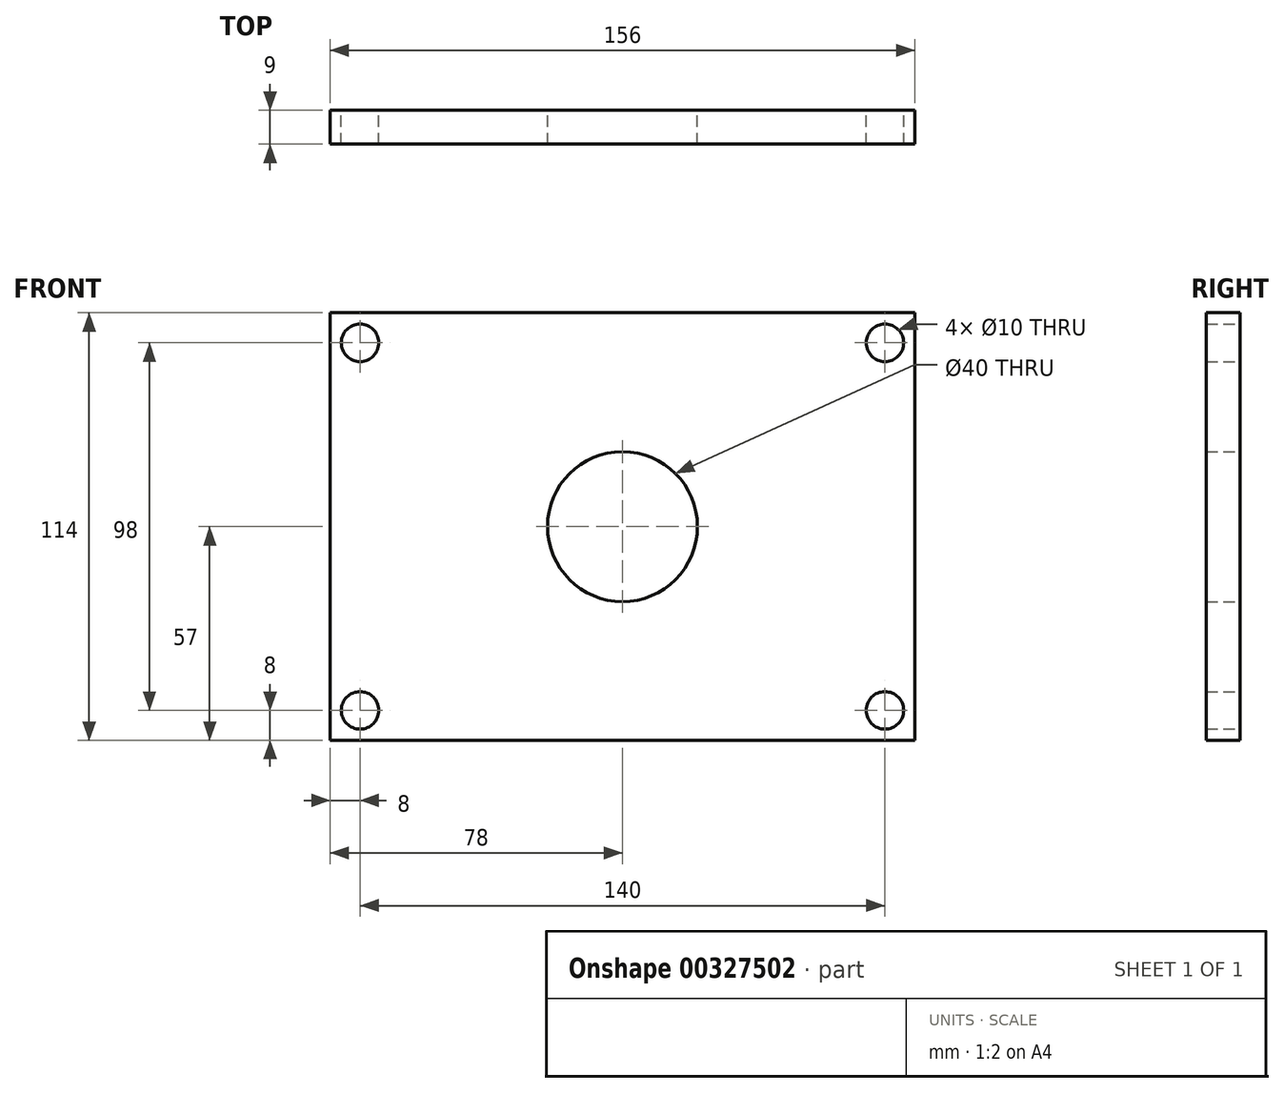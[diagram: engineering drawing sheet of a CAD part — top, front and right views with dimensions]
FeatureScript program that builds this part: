
annotation { "Feature Type Name" : "Feature", "Feature Type Description" : "" }
export const myFeature = defineFeature(function(context is Context, id is Id, definition is map)
    precondition{}
    {
        {
            var Q0;
            Q0=qCreatedBy(makeId("Front.planeOp"),FACE);
            var sketch = newSketch(context, id + "F0", { "sketchPlane" : qUnion([Q0])});
            skCircle(sketch, "E0", {"center": v(0, 0) * mm, "radius": 20 * mm});
            skLineSegment(sketch, "E1.bottom", {"start": v(-78, -57) * mm, "end": v(78, -57) * mm});
            skLineSegment(sketch, "E1.top", {"start": v(-78, 57) * mm, "end": v(78, 57) * mm});
            skLineSegment(sketch, "E1.left", {"start": v(-78, -57) * mm, "end": v(-78, 57) * mm});
            skLineSegment(sketch, "E1.right", {"start": v(78, -57) * mm, "end": v(78, 57) * mm});
            skLineSegment(sketch, "E2", {"start": v(-78, 57) * mm, "end": v(-78, 52) * mm});
            skLineSegment(sketch, "E3.MirrorCS", {"start": v(78, 57) * mm, "end": v(-78, 57) * mm});
            skLineSegment(sketch, "E4.MirrorCS", {"start": v(78, 57) * mm, "end": v(78, 52) * mm});
            skLineSegment(sketch, "E5.MirrorCS", {"start": v(78, -57) * mm, "end": v(78, -52) * mm});
            skLineSegment(sketch, "E6.MirrorCS", {"start": v(-78, -57) * mm, "end": v(-78, -52) * mm});
            skLineSegment(sketch, "E7.MirrorCS", {"start": v(78, -57) * mm, "end": v(-78, -57) * mm});
            skLineSegment(sketch, "E8.bottom", {"start": v(-70, 49) * mm, "end": v(70, 49) * mm, "construction": true});
            skLineSegment(sketch, "E8.top", {"start": v(-70, -49) * mm, "end": v(70, -49) * mm, "construction": true});
            skLineSegment(sketch, "E8.left", {"start": v(-70, 49) * mm, "end": v(-70, -49) * mm, "construction": true});
            skLineSegment(sketch, "E8.right", {"start": v(70, 49) * mm, "end": v(70, -49) * mm, "construction": true});
            skCircle(sketch, "E9", {"center": v(70, 49) * mm, "radius": 5 * mm});
            skCircle(sketch, "E10", {"center": v(-70, 49) * mm, "radius": 5 * mm});
            skCircle(sketch, "E11", {"center": v(70, -49) * mm, "radius": 5 * mm});
            skCircle(sketch, "E12", {"center": v(-70, -49) * mm, "radius": 5 * mm});
            skSolve(sketch);
        }
        {
            var Q0;
            Q0 = qSketchRegion(id + "F0", true);
            extrude(context, id + "F1", {"entities" : qUnion([Q0]), "depth" : 9 * mm});
        }
    });
